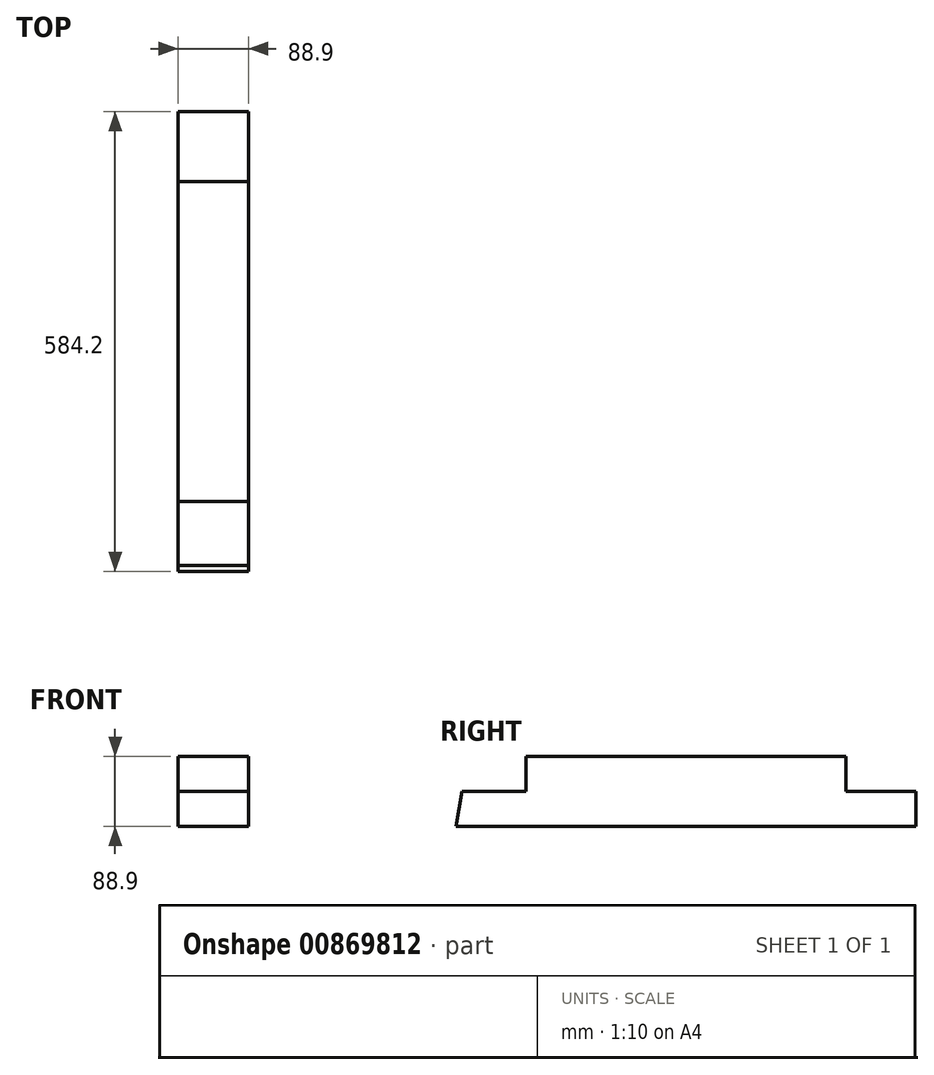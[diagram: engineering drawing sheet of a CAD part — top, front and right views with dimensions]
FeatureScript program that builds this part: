
annotation { "Feature Type Name" : "Feature", "Feature Type Description" : "" }
export const myFeature = defineFeature(function(context is Context, id is Id, definition is map)
    precondition{}
    {
        {
            var Q0;
            Q0=qCreatedBy(makeId("Front.planeOp"),FACE);
            var sketch = newSketch(context, id + "F0", { "sketchPlane" : qUnion([Q0])});
            skLineSegment(sketch, "E0.bottom", {"start": v(44.45, -44.45) * mm, "end": v(-44.45, -44.45) * mm});
            skLineSegment(sketch, "E0.top", {"start": v(44.45, 44.45) * mm, "end": v(-44.45, 44.45) * mm});
            skLineSegment(sketch, "E0.left", {"start": v(44.45, -44.45) * mm, "end": v(44.45, 44.45) * mm});
            skLineSegment(sketch, "E0.right", {"start": v(-44.45, -44.45) * mm, "end": v(-44.45, 44.45) * mm});
            skPoint(sketch, "E0.middle", {"position": v(0, 0) * mm});
            skSolve(sketch);
        }
        {
            var Q0;
            Q0 = qSketchRegion(id + "F0", true);
            extrude(context, id + "F1", {"entities" : qUnion([Q0]), "oppositeDirection" : true, "depth" : 584.2 * mm, "offsetDistance" : 25.4 * mm});
        }
        {
            var Q0;
            Q0=makeQuery(id+"F1.opExtrude","SWEPT_FACE",FACE,{"disambiguationData":[OSD([sQuery(id+"F0.wireOp",EDGE,"E0.left")])]});
            var sketch = newSketch(context, id + "F2", { "sketchPlane" : qUnion([Q0])});
            skLineSegment(sketch, "E1.bottom", {"start": v(0, 44.45) * mm, "end": v(88.9, 44.45) * mm});
            skLineSegment(sketch, "E1.top", {"start": v(0, 0) * mm, "end": v(88.9, 0) * mm});
            skLineSegment(sketch, "E1.left", {"start": v(0, 44.45) * mm, "end": v(0, 0) * mm});
            skLineSegment(sketch, "E1.right", {"start": v(88.9, 44.45) * mm, "end": v(88.9, 0) * mm});
            skLineSegment(sketch, "E2.bottom", {"start": v(584.2, 44.45) * mm, "end": v(495.3, 44.45) * mm});
            skLineSegment(sketch, "E2.top", {"start": v(584.2, 0) * mm, "end": v(495.3, 0) * mm});
            skLineSegment(sketch, "E2.left", {"start": v(584.2, 44.45) * mm, "end": v(584.2, 0) * mm});
            skLineSegment(sketch, "E2.right", {"start": v(495.3, 44.45) * mm, "end": v(495.3, 0) * mm});
            skSolve(sketch);
        }
        {
            var Q0;
            Q0 = qSketchRegion(id + "F2", true);
            extrude(context, id + "F3", {"entities" : qUnion([Q0]), "operationType" : NewBodyOperationType.REMOVE, "endBound" : BoundingType.THROUGH_ALL, "oppositeDirection" : true, "depth" : 25.4 * mm, "offsetDistance" : 25.4 * mm});
        }
        {
            var Q0;
            Q0=makeQuery(id+"F1.opExtrude","SWEPT_FACE",FACE,{"disambiguationData":[OSD([sQuery(id+"F0.wireOp",EDGE,"E0.left")])]});
            var sketch = newSketch(context, id + "F4", { "sketchPlane" : qUnion([Q0])});
            skLineSegment(sketch, "E3", {"start": v(0, -44.45) * mm, "end": v(7.84, 0) * mm});
            skLineSegment(sketch, "E4", {"start": v(7.84, 0) * mm, "end": v(0, 0) * mm});
            skLineSegment(sketch, "E5", {"start": v(0, 0) * mm, "end": v(0, -44.45) * mm});
            skSolve(sketch);
        }
        {
            var Q0;
            Q0 = qSketchRegion(id + "F4", true);
            extrude(context, id + "F5", {"entities" : qUnion([Q0]), "operationType" : NewBodyOperationType.REMOVE, "endBound" : BoundingType.THROUGH_ALL, "oppositeDirection" : true, "depth" : 25.4 * mm, "offsetDistance" : 25.4 * mm});
        }
    });
